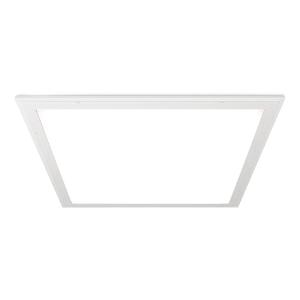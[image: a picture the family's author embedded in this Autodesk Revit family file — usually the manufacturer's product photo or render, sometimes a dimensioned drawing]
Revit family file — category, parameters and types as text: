
# Revit family: 3f_filippi_-_l_650_luce_diffusa_vss_3f_filippi_-_21881_-_l_650_42w-840_dali_vss_596x596
name_source: partatom
category: Lighting Fixtures
units: mm (PartAtom-declared; Revit-internal decimal feet)

## family parameters
Cut with Voids When Loaded = No
Host = Face
Light Source = No
Part Type = Normal
Room Calculation Point = No
Round Connector Dimension = Use Diameter
Shared = No

## types (1)
- 3F Filippi - L 650 Luce Diffusa VSS (1 x LED, 4965 lm, 47 W, 4000 K)
    Apparent Load = 47 VA
    Approval mark = ENEC
    CIE Flux Codes = 63 92 98 100 100
    Color Rendering = 80
    Color Temperature = 4000 K
    Control Gear = Electronic transformer
    Default Elevation = 1800 mm
    Description = ILLUMINOTECHNICAL
Luminous efficiency 100% (DLOR 100%, ULOR 0%).
Initial luminous flux of the luminaire 4965 lm.
Direct symmetric distribution.
Installation Interdistance Transv.D = 1.17 x hu - Long.D = 1.16 x hu.
Average luminance <3000 cd/m² for radial angles >65°.
Tabular UGR (CIE 117 - 4H-8H; S=0.25H; 70/50/20): RUG 18.1 - 18.
Beam angle: 90° - 88°.
Luminous efficacy 106 lm/W.
Lifetime (L93/B10): 30000 h. (tq+25°C)
Lifetime (L90/B10): 50000 h. (tq+25°C)
Lifetime (L85/B10): 80000 h. (tq+25°C)
Lifetime (L80/B10): 100000 h. (tq+25°C)
Sudden decreased luminous flux after 50000 hours: 0% (C0).
Photobiological safety in compliance with IEC/TR 62778: RG0 risk exempt, (IEC 62471).
In compliance with IEC/EN 62722-2-1 - IEC/EN 62717 standards.

SOURCE
Squared LED module 42W/840.
Source with special protection against aggressive chemically-volatile substances for standard LED technology.
Energy efficiency class (UE 2019/2020 - UE 2019/2015): D.
CIE 13.3 Colour rendering index: CRI >80 (R9 <50%).
IES TM-30 Fidelity Index: Rf = 84 Rg = 95.
CCT nominal colour temperature 4000 K.
Colour initial tolerance (MacAdam): SDCM 3.

MECHANICAL
Housing in galvannealed steel, painted in white epoxy-polyester.
Perimetral frame in white stainless steel.
VSS moulded laminated dipped glass, non-combustible, thickness 7 mm.
Anti-glare opal polycarbonate filter for brightness uniformity.
Luminaire with limited surface temperature. - D - (EN 60598-2-24)
Dimensions: 596x596 mm, height 90 mm. Weight 9.7 kg.
IP66 protection degree for exposed part, IP64 for recessed part.
Mechanical strength to impacts IK08 (5 joule).
Glow-wire test resistance 650°C.

ELECTRICAL
Halogen Free DALI-2 DATI (Parts 251, 252, 253), PUSH-DIM, electronic wiring 230V-50/60Hz, power factor 0.95 at full load, THD <25%, constant output current, SELV, class I, 1 driver, 1 DALI addresse.
Power of the luminaire 47 W.
CE - IEC 60598-1 - EN 60598-1.
SAFE FLICKER: PstLM=<1 and SVM=<0.4 (IEC TR 61547-1 and IEC TR 63158), to ensure a more comfortable and safe light.
Luminaire compliant with EN 60598-2-22 for power supply from a centralised emergency system CPSS (Central Power Supply System), not incorporated in the luminaire - high risk areas excluded. The default power and flux are 100% in AC and 15% in DC.
Ambient temperature from 0°C to +40°C.
Temperature class T6 max 85°C.
5-pole terminal block (L-N-PE-DA/DA) quick connection for line connection with connection capacity 2x2.5 mm² per poles.
Relative humidity UR: <85%.

INSTALLATION
Lay-in recessed fitting.
All accessories dedicated to this product are available on the Catalog and on our website www.3F-Filippi.com.

APPLICATIONS
Suitable product for food production plants (HACCP), IFS (Food Version 6), BRC (GSFS Food Version 7).
Environments: hospital premises, transit areas, laboratories, platform-roof, underpasses.
Environments: sterilized, aseptic.
In hospital environments, food industry or machines with parts in motion, with considerable sudden temperature changes, and in general in any environments requiring total protection against falling fragments, use luminaires with laminated glass only.
Tempered glass is not immune to falling fragments from harmless and caused by shocks or exceptionally derived from the tempering process.
Environments requiring a high level of protection and simplified cleaning.
Environments with exacting visual tasks, where diffused soft light for optimum visual comfort is required.

LIGHT MANAGEMENT
Recommended minimum setting: 10%.
The luminaire, equipped with (DALI-2 DATI) driver, can be controlled manually with 3F Easy Dim technology or automatically/manually with wired or wireless DALI/D2D control systems.
The D2D driver guarantees interoperability with other devices with the same certification by making the following information available:
Device Data (Part 251), Energy Report (Part 252), Diagnosis & Maintenance (Part 253).
In electrical systems without a regulation system (manual or automatic) and DALI bus, a suitable jumper must be made on the DA-DA terminals of the appliance.

WARNING
Luminaire designed for disposal/recycling at end-of-life.
Replaceable (LED only) light source by a professional. Replaceable control gear by a professional.
    Height = 0 mm  [stored 0 ft]
    Lamp = 1 x LED
    Lamp Light Flux = 4965 lm
    Lamp Power = 47 W
    Lamp count = 1
    Length = 596 mm
    Lifetime = 50000 h
    Luminous efficacy = 106 lm/W
    Manufacturer = 3F Filippi
    ModVariant = No
    Model = 3F Filippi - 21881 - L 650 42W-840 DALI VSS 596x596
    Mounting Place = Ceiling
    Mounting Type = Recessed
    Number of Poles = 1
    OnlyDefault = Yes
    Power Factor = 1
    Product Name = 3F Filippi - L 650 Luce Diffusa VSS
    Product group = recessed luminaire
    ProductGroupID = 4
    Protection Class = Protection class I
    Protection Degree = IP 64
    RLX_Detail_Level = 1
    RLX_Emergency_Light_Flux = 0 lm
    RLX_Emergency_Type = 0
    RLX_Emergency_Type_DB = No
    RlxData = <blob elided: 101293 chars, md5=6e1943c8>
    Socket = socket
    Standby Power = 0 W
    System Light Flux = 4965 lm
    System Power = 47 W
    Type Comments = Product without accessories
    Type Image = 3ffilippi_l_650_luce_diffusa_vss.jpg
    URL = http://relux.com
    VarID = ---
    Voltage = 0 V
    Weight = 0.00 kg
    Width = 596 mm

note: [stored X ft] marks values corroborated as IEEE doubles in the binary element streams (Revit-internal decimal feet)

## geometry (parser evidence)
native form markers: Blend x4, Sweep x11
no freeform markers — native parametric forms only
